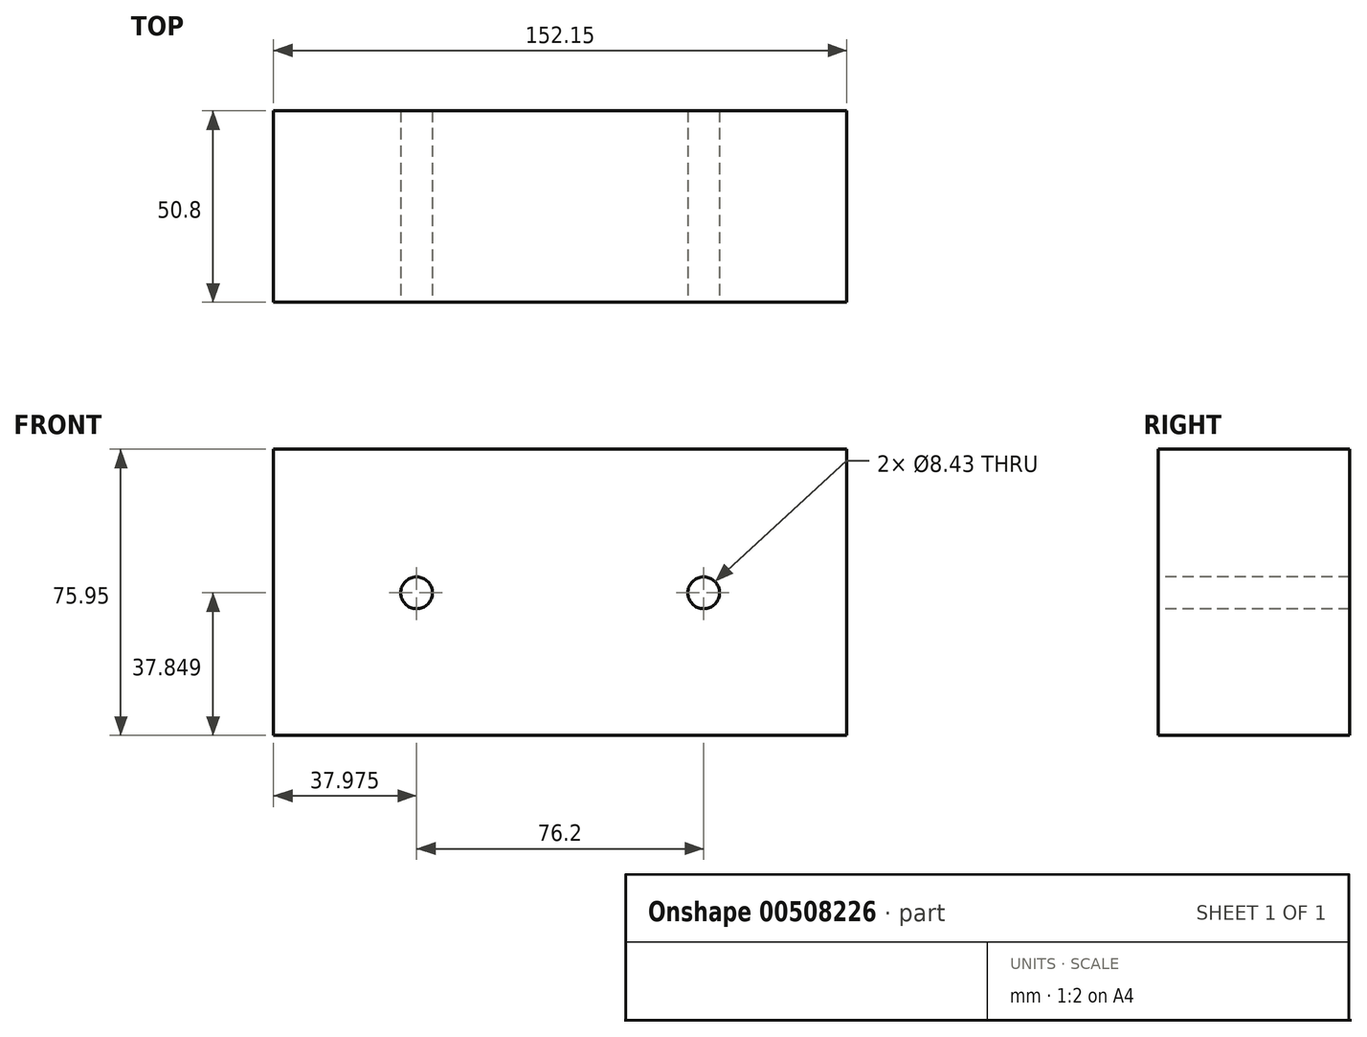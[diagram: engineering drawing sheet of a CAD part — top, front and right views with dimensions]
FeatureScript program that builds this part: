
annotation { "Feature Type Name" : "Feature", "Feature Type Description" : "" }
export const myFeature = defineFeature(function(context is Context, id is Id, definition is map)
    precondition{}
    {
        {
            var Q0;
            Q0=qCreatedBy(makeId("Front.planeOp"),FACE);
            var sketch = newSketch(context, id + "F0", { "sketchPlane" : qUnion([Q0])});
            skLineSegment(sketch, "E0.bottom", {"start": v(-83.87, 35.37) * mm, "end": v(68.28, 35.37) * mm});
            skLineSegment(sketch, "E0.top", {"start": v(-83.87, -40.58) * mm, "end": v(68.28, -40.58) * mm});
            skLineSegment(sketch, "E0.left", {"start": v(-83.87, 35.37) * mm, "end": v(-83.87, -40.58) * mm});
            skLineSegment(sketch, "E0.right", {"start": v(68.28, 35.37) * mm, "end": v(68.28, -40.58) * mm});
            skSolve(sketch);
        }
        {
            var Q0;
            Q0=makeQuery(id+"F0.imprint","IMPRINT",FACE,{"disambiguationData":[TD([[makeQuery(id+"F0.imprint","IMPRINT",EDGE,{"derivedFrom":sQuery(id+"F0.wireOp",EDGE,"E0.bottom")}),-1.0]])]});
            extrude(context, id + "F1", {"entities" : qUnion([Q0]), "depth" : 50.8 * mm});
        }
        {
            var Q0;
            Q0=makeQuery(id+"F1.opExtrude","CAP_FACE",FACE,{"disambiguationData":[OSD([sQuery(id+"F0.wireOp",EDGE,"E0.bottom"),sQuery(id+"F0.wireOp",EDGE,"E0.top"),sQuery(id+"F0.wireOp",EDGE,"E0.left"),sQuery(id+"F0.wireOp",EDGE,"E0.right")])],"isStart":false});
            var sketch = newSketch(context, id + "F2", { "sketchPlane" : qUnion([Q0])});
            skPoint(sketch, "E1", {"position": v(-45.9, -2.73) * mm});
            skPoint(sketch, "E2", {"position": v(30.3, -2.73) * mm});
            skSolve(sketch);
        }
        {
            var Q0;
            Q0=sQuery(id+"F2.wireOp",VERTEX,"E1");
            var Q1;
            Q1=sQuery(id+"F2.wireOp",VERTEX,"E2");
            var Q2;
            Q2=makeQuery(id+"F1.opExtrude","SWEPT_BODY",BODY,{"disambiguationData":[OSD([sQuery(id+"F0.wireOp",EDGE,"E0.bottom"),sQuery(id+"F0.wireOp",EDGE,"E0.top"),sQuery(id+"F0.wireOp",EDGE,"E0.left"),sQuery(id+"F0.wireOp",EDGE,"E0.right")])]});
            hole(context, id + "F3", {"style" : HoleStyle.SIMPLE, "endStyle" : HoleEndStyle.THROUGH, "standardTappedOrClearance" : lookupTablePath({ "standard" : "ANSI", "fit" : "Normal (ASME)", "size" : "5/16", "type" : "Clearance" }), "standardBlindInLast" : lookupTablePath({ "fit" : "Free", "standard" : "ANSI", "size" : "5/16", "type" : "Clearance" }), "holeDiameter" : 8.43 * mm, "isTappedThrough" : true, "tappedDepth" : 12.7 * mm, "tapClearance" : 3, "startFromSketch" : true, "locations" : qUnion([Q0, Q1]), "scope" : qUnion([Q2])});
        }
    });
